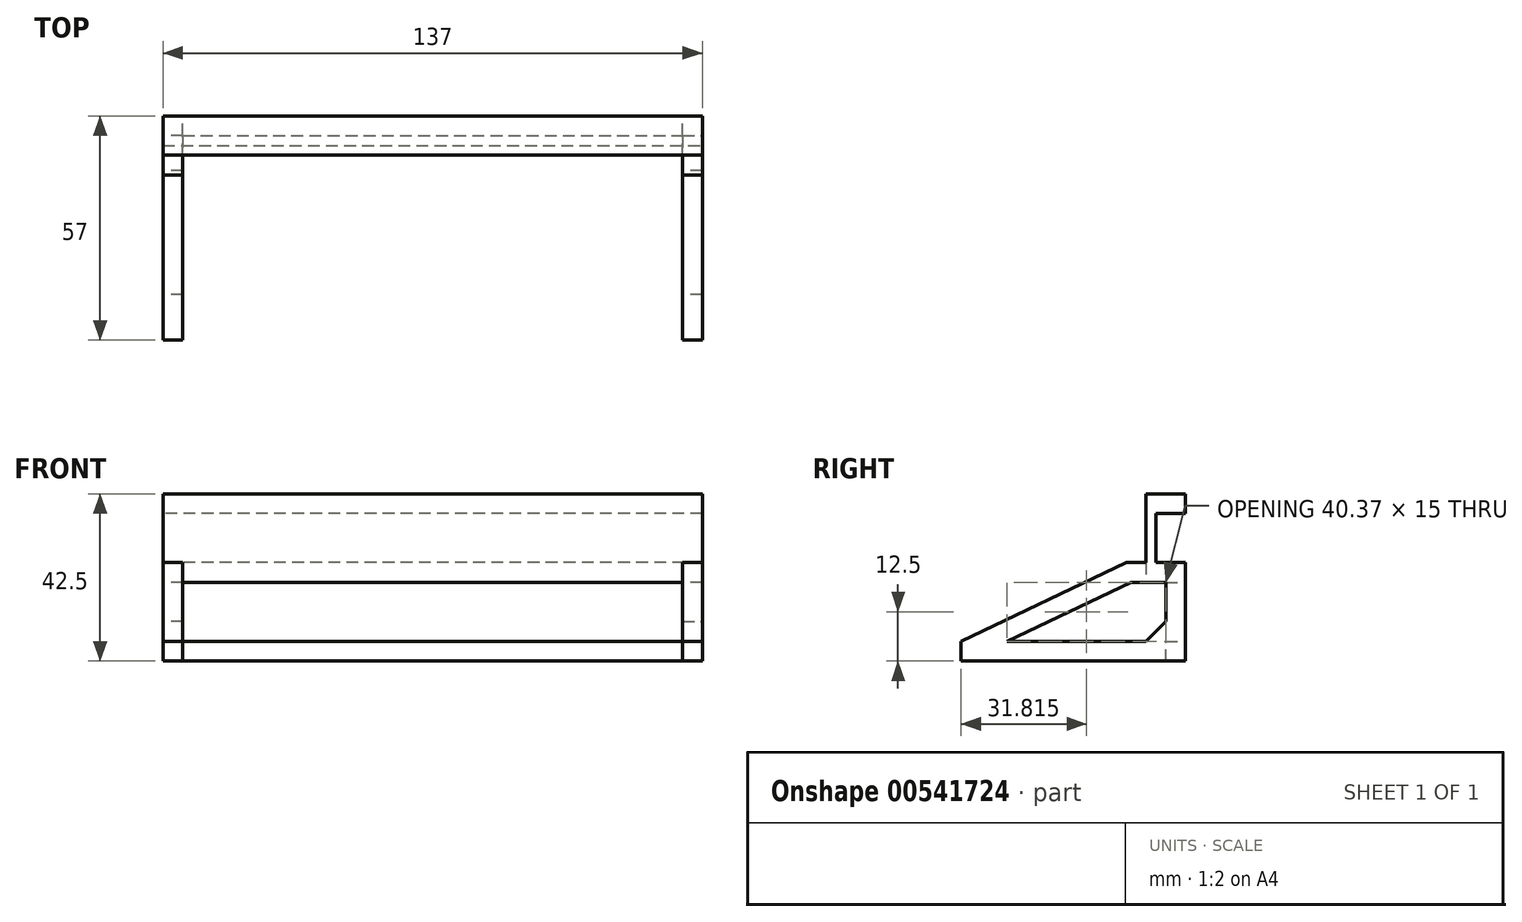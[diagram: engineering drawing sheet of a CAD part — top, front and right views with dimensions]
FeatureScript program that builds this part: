
annotation { "Feature Type Name" : "Feature", "Feature Type Description" : "" }
export const myFeature = defineFeature(function(context is Context, id is Id, definition is map)
    precondition{}
    {
        {
            var Q0;
            Q0=qCreatedBy(makeId("Top.planeOp"),FACE);
            var sketch = newSketch(context, id + "F0", { "sketchPlane" : qUnion([Q0])});
            skLineSegment(sketch, "E0.bottom", {"start": v(68.5, 30) * mm, "end": v(-68.5, 30) * mm});
            skLineSegment(sketch, "E0.top", {"start": v(68.5, -30) * mm, "end": v(-68.5, -30) * mm});
            skLineSegment(sketch, "E0.left", {"start": v(68.5, 30) * mm, "end": v(68.5, -30) * mm});
            skLineSegment(sketch, "E0.right", {"start": v(-68.5, 30) * mm, "end": v(-68.5, -30) * mm});
            skPoint(sketch, "E0.middle", {"position": v(0, 0) * mm});
            skPoint(sketch, "E1", {"position": v(-63.5, 25) * mm});
            skPoint(sketch, "E2", {"position": v(63.5, -25) * mm});
            skLineSegment(sketch, "E3.bottom", {"start": v(-63.5, 25) * mm, "end": v(63.5, 25) * mm});
            skLineSegment(sketch, "E3.top", {"start": v(-63.5, -25) * mm, "end": v(63.5, -25) * mm});
            skLineSegment(sketch, "E3.left", {"start": v(-63.5, 25) * mm, "end": v(-63.5, -25) * mm});
            skLineSegment(sketch, "E3.right", {"start": v(63.5, 25) * mm, "end": v(63.5, -25) * mm});
            skSolve(sketch);
        }
        {
            var Q0;
            Q0=makeQuery(id+"F0.imprint","IMPRINT",FACE,{"disambiguationData":[TD([[makeQuery(id+"F0.imprint","IMPRINT",EDGE,{"derivedFrom":sQuery(id+"F0.wireOp",EDGE,"E0.bottom")}),1.0]])]});
            extrude(context, id + "F1", {"entities" : qUnion([Q0]), "depth" : 25 * mm, "offsetDistance" : 25 * mm});
        }
        {
            var Q0;
            Q0=makeQuery(id+"F1.opExtrude","SWEPT_FACE",FACE,{"disambiguationData":[OSD([sQuery(id+"F0.wireOp",EDGE,"E0.right")])]});
            var sketch = newSketch(context, id + "F2", { "sketchPlane" : qUnion([Q0])});
            skPoint(sketch, "E4", {"position": v(30, 5) * mm});
            skPoint(sketch, "E5", {"position": v(-25, 25) * mm});
            skLineSegment(sketch, "E6", {"start": v(-25, 25) * mm, "end": v(30, 5) * mm});
            skSolve(sketch);
        }
        {
            var Q0;
            {var subQ0=sQuery(id+"F2.wireOp",EDGE,"E6");Q0=makeQuery(id+"F2.imprint","IMPRINT",FACE,{"disambiguationData":[TD([[makeQuery(id+"F2.imprint","IMPRINT",EDGE,{"derivedFrom":subQ0}),1.0]])]});}
            extrude(context, id + "F3", {"entities" : qUnion([Q0]), "operationType" : NewBodyOperationType.REMOVE, "endBound" : BoundingType.THROUGH_ALL, "oppositeDirection" : true, "depth" : 25 * mm, "offsetDistance" : 25 * mm});
        }
        {
            var Q0;
            Q0=makeQuery(id+"F1.opExtrude","SWEPT_FACE",FACE,{"disambiguationData":[OSD([sQuery(id+"F0.wireOp",EDGE,"E0.bottom")])]});
            extrude(context, id + "F4", {"entities" : qUnion([Q0]), "operationType" : NewBodyOperationType.ADD, "depth" : 10 * mm, "offsetDistance" : 25 * mm});
        }
        {
            var Q0;
            {var subQ0=sQuery(id+"F0.wireOp",EDGE,"E0.bottom");Q0=makeQuery(id+"F4.boolean.opBoolean","MERGE",FACE,{"derivedFrom":[makeQuery(id+"F1.opExtrude","CAP_FACE",FACE,{"disambiguationData":[OSD([subQ0,sQuery(id+"F0.wireOp",EDGE,"E0.top"),sQuery(id+"F0.wireOp",EDGE,"E0.left"),sQuery(id+"F0.wireOp",EDGE,"E0.right"),sQuery(id+"F0.wireOp",EDGE,"E3.bottom"),sQuery(id+"F0.wireOp",EDGE,"E3.top"),sQuery(id+"F0.wireOp",EDGE,"E3.left"),sQuery(id+"F0.wireOp",EDGE,"E3.right")])],"isStart":false}),makeQuery(id+"F4.opExtrude","SWEPT_FACE",FACE,{"disambiguationData":[OSD([subQ0]),TDD([makeQuery(id+"F1.opExtrude","CAP_EDGE",EDGE,{"disambiguationData":[OSD([subQ0])],"isStart":false})])]})]});}
            var sketch = newSketch(context, id + "F5", { "sketchPlane" : qUnion([Q0])});
            skPoint(sketch, "E7", {"position": v(-68.5, 32.5) * mm});
            skLineSegment(sketch, "E8", {"start": v(-68.5, 32.5) * mm, "end": v(68.5, 32.5) * mm});
            skSolve(sketch);
        }
        {
            var Q0;
            {var subQ13=sQuery(id+"F5.wireOp",EDGE,"E8");Q0=makeQuery(id+"F5.imprint","IMPRINT",FACE,{"disambiguationData":[TD([[makeQuery(id+"F5.imprint","IMPRINT",EDGE,{"derivedFrom":subQ13}),-1.0]])]});}
            extrude(context, id + "F6", {"entities" : qUnion([Q0]), "operationType" : NewBodyOperationType.ADD, "depth" : 17.5 * mm, "offsetDistance" : 25 * mm});
        }
        {
            var Q0;
            Q0=makeQuery(id+"F6.opExtrude","SWEPT_FACE",FACE,{"disambiguationData":[OSD([sQuery(id+"F5.wireOp",EDGE,"E8")])]});
            var sketch = newSketch(context, id + "F7", { "sketchPlane" : qUnion([Q0])});
            skPoint(sketch, "E9", {"position": v(-68.5, 37.5) * mm});
            skLineSegment(sketch, "E10.bottom", {"start": v(-68.5, 37.5) * mm, "end": v(68.5, 37.5) * mm});
            skLineSegment(sketch, "E10.top", {"start": v(-68.5, 42.5) * mm, "end": v(68.5, 42.5) * mm});
            skLineSegment(sketch, "E10.left", {"start": v(-68.5, 37.5) * mm, "end": v(-68.5, 42.5) * mm});
            skLineSegment(sketch, "E10.right", {"start": v(68.5, 37.5) * mm, "end": v(68.5, 42.5) * mm});
            skSolve(sketch);
        }
        {
            var Q0;
            Q0=makeQuery(id+"F7.imprint","IMPRINT",FACE,{"disambiguationData":[TD([[makeQuery(id+"F7.imprint","IMPRINT",EDGE,{"derivedFrom":sQuery(id+"F7.wireOp",EDGE,"E10.bottom")}),1.0]])]});
            var Q1;
            Q1=makeQuery(id+"F4.opExtrude","CAP_FACE",FACE,{"disambiguationData":[OSD([sQuery(id+"F0.wireOp",EDGE,"E0.bottom")])],"isStart":false});
            extrude(context, id + "F8", {"entities" : qUnion([Q0]), "operationType" : NewBodyOperationType.ADD, "endBound" : BoundingType.UP_TO_SURFACE, "depth" : 25 * mm, "endBoundEntityFace" : qUnion([Q1]), "offsetDistance" : 25 * mm});
        }
        {
            var Q0;
            Q0=makeQuery(id+"F4.opExtrude","CAP_FACE",FACE,{"disambiguationData":[OSD([sQuery(id+"F0.wireOp",EDGE,"E0.bottom")])],"isStart":false});
            var sketch = newSketch(context, id + "F9", { "sketchPlane" : qUnion([Q0])});
            skPoint(sketch, "E11", {"position": v(-63.5, 20) * mm});
            skPoint(sketch, "E12", {"position": v(63.5, 5) * mm});
            skLineSegment(sketch, "E13.bottom", {"start": v(-63.5, 20) * mm, "end": v(63.5, 20) * mm});
            skLineSegment(sketch, "E13.top", {"start": v(-63.5, 5) * mm, "end": v(63.5, 5) * mm});
            skLineSegment(sketch, "E13.left", {"start": v(-63.5, 20) * mm, "end": v(-63.5, 5) * mm});
            skLineSegment(sketch, "E13.right", {"start": v(63.5, 20) * mm, "end": v(63.5, 5) * mm});
            skSolve(sketch);
        }
        {
            var Q0;
            {var subQ0=sQuery(id+"F0.wireOp",EDGE,"E0.left");var subQ1=sQuery(id+"F0.wireOp",EDGE,"E0.bottom");Q0=makeQuery(id+"F8.boolean.opBoolean","MERGE",FACE,{"derivedFrom":[makeQuery(id+"F6.boolean.opBoolean","MERGE",FACE,{"derivedFrom":[makeQuery(id+"F4.boolean.opBoolean","MERGE",FACE,{"derivedFrom":[makeQuery(id+"F1.opExtrude","SWEPT_FACE",FACE,{"disambiguationData":[OSD([subQ0])]}),makeQuery(id+"F4.opExtrude","SWEPT_FACE",FACE,{"disambiguationData":[OSD([subQ1,subQ0])]})]}),makeQuery(id+"F6.opExtrude","SWEPT_FACE",FACE,{"disambiguationData":[OSD([subQ1,subQ0])]})]}),makeQuery(id+"F8.opExtrude","SWEPT_FACE",FACE,{"disambiguationData":[OSD([sQuery(id+"F7.wireOp",EDGE,"E10.left")])]})]});}
            var sketch = newSketch(context, id + "F10", { "sketchPlane" : qUnion([Q0])});
            skPoint(sketch, "E14", {"position": v(-17, 0) * mm});
            skLineSegment(sketch, "E15", {"start": v(-17, 0) * mm, "end": v(-17, 9.73) * mm});
            skSolve(sketch);
        }
        {
            var Q0;
            {var subQ0=sQuery(id+"F10.wireOp",EDGE,"E15");Q0=makeQuery(id+"F10.imprint","IMPRINT",FACE,{"disambiguationData":[TD([[makeQuery(id+"F10.imprint","IMPRINT",EDGE,{"derivedFrom":subQ0}),1.0]])]});}
            extrude(context, id + "F11", {"entities" : qUnion([Q0]), "operationType" : NewBodyOperationType.REMOVE, "endBound" : BoundingType.THROUGH_ALL, "oppositeDirection" : true, "depth" : 25 * mm, "offsetDistance" : 25 * mm});
        }
        {
            var Q0;
            {var subQ3=sQuery(id+"F0.wireOp",EDGE,"E3.bottom");var subQ4=sQuery(id+"F0.wireOp",EDGE,"E0.right");Q0=makeQuery(id+"FVMJIEAKdRelkvC_1.boolean.opBoolean","SPLIT",FACE,{"disambiguationData":[TD([makeQuery(id+"FVMJIEAKdRelkvC_1.opExtrude","SWEPT_FACE",FACE,{"disambiguationData":[OSD([sQuery(id+"Ff6jXWaRgxi8vil_1.wireOp",EDGE,"BFvBPHGJ-g1eL-yhey-g6Zf-fKgrT3vlxnNi")])]})])],"derivedFrom":makeQuery(id+"F6.boolean.opBoolean","MERGE",FACE,{"derivedFrom":[makeQuery(id+"F1.opExtrude","SWEPT_FACE",FACE,{"disambiguationData":[OSD([subQ3])]}),makeQuery(id+"F6.opExtrude","SWEPT_FACE",FACE,{"disambiguationData":[OSD([subQ4,subQ3,sQuery(id+"F2.wireOp",EDGE,"E6")])]})]})});}
            extrude(context, id + "F12", {"entities" : qUnion([Q0]), "operationType" : NewBodyOperationType.REMOVE, "oppositeDirection" : true, "depth" : 5 * mm, "offsetDistance" : 25 * mm});
        }
        {
            var Q0;
            {var subQ0=sQuery(id+"F0.wireOp",EDGE,"E0.right");var subQ1=sQuery(id+"F0.wireOp",EDGE,"E0.bottom");Q0=makeQuery(id+"F8.boolean.opBoolean","MERGE",FACE,{"derivedFrom":[makeQuery(id+"F6.boolean.opBoolean","MERGE",FACE,{"derivedFrom":[makeQuery(id+"F4.boolean.opBoolean","MERGE",FACE,{"derivedFrom":[makeQuery(id+"F1.opExtrude","SWEPT_FACE",FACE,{"disambiguationData":[OSD([subQ0])]}),makeQuery(id+"F4.opExtrude","SWEPT_FACE",FACE,{"disambiguationData":[OSD([subQ1,subQ0])]})]}),makeQuery(id+"F6.opExtrude","SWEPT_FACE",FACE,{"disambiguationData":[OSD([subQ1,subQ0])]})]}),makeQuery(id+"F8.opExtrude","SWEPT_FACE",FACE,{"disambiguationData":[OSD([sQuery(id+"F7.wireOp",EDGE,"E10.right")])]})]});}
            var sketch = newSketch(context, id + "F13", { "sketchPlane" : qUnion([Q0])});
            skPoint(sketch, "E16", {"position": v(17, 5) * mm});
            skLineSegment(sketch, "E17", {"start": v(17, 5) * mm, "end": v(-25, 25) * mm});
            skSolve(sketch);
        }
        {
            var Q0;
            {var subQ0=sQuery(id+"F13.wireOp",EDGE,"E17");Q0=makeQuery(id+"F13.imprint","IMPRINT",FACE,{"disambiguationData":[TD([[makeQuery(id+"F13.imprint","IMPRINT",EDGE,{"derivedFrom":subQ0}),-1.0]])]});}
            extrude(context, id + "F14", {"entities" : qUnion([Q0]), "operationType" : NewBodyOperationType.REMOVE, "endBound" : BoundingType.THROUGH_ALL, "oppositeDirection" : true, "depth" : 25 * mm, "offsetDistance" : 25 * mm});
        }
        {
            var Q0;
            Q0=makeQuery(id+"F9.imprint","IMPRINT",FACE,{"disambiguationData":[TD([[makeQuery(id+"F9.imprint","IMPRINT",EDGE,{"derivedFrom":sQuery(id+"F9.wireOp",EDGE,"E13.bottom")}),-1.0]])]});
            extrude(context, id + "F15", {"entities" : qUnion([Q0]), "operationType" : NewBodyOperationType.REMOVE, "endBound" : BoundingType.THROUGH_ALL, "oppositeDirection" : true, "depth" : 25 * mm, "offsetDistance" : 25 * mm});
        }
        {
            var Q0;
            {var subQ0=sQuery(id+"F0.wireOp",EDGE,"E0.right");var subQ1=sQuery(id+"F0.wireOp",EDGE,"E0.bottom");Q0=makeQuery(id+"F8.boolean.opBoolean","MERGE",FACE,{"derivedFrom":[makeQuery(id+"F6.boolean.opBoolean","MERGE",FACE,{"derivedFrom":[makeQuery(id+"F4.boolean.opBoolean","MERGE",FACE,{"derivedFrom":[makeQuery(id+"F1.opExtrude","SWEPT_FACE",FACE,{"disambiguationData":[OSD([subQ0])]}),makeQuery(id+"F4.opExtrude","SWEPT_FACE",FACE,{"disambiguationData":[OSD([subQ1,subQ0])]})]}),makeQuery(id+"F6.opExtrude","SWEPT_FACE",FACE,{"disambiguationData":[OSD([subQ1,subQ0])]})]}),makeQuery(id+"F8.opExtrude","SWEPT_FACE",FACE,{"disambiguationData":[OSD([sQuery(id+"F7.wireOp",EDGE,"E10.right")])]})]});}
            var sketch = newSketch(context, id + "F16", { "sketchPlane" : qUnion([Q0])});
            skPoint(sketch, "E18", {"position": v(16.01, 1.09) * mm});
            skPoint(sketch, "E19", {"position": v(-9.28, 11.97) * mm});
            skLineSegment(sketch, "E20", {"start": v(-9.28, 11.97) * mm, "end": v(-36.63, 25) * mm});
            skLineSegment(sketch, "E21", {"start": v(-9.28, 11.97) * mm, "end": v(15.87, 0) * mm});
            skPoint(sketch, "E22", {"position": v(-35, 20) * mm});
            skPoint(sketch, "E23", {"position": v(-35, 5) * mm});
            skLineSegment(sketch, "E24", {"start": v(-35, 5) * mm, "end": v(5.37, 5) * mm});
            skLineSegment(sketch, "E25", {"start": v(-35, 5) * mm, "end": v(-35, 20) * mm});
            skLineSegment(sketch, "E26", {"start": v(-35, 20) * mm, "end": v(-26.13, 20) * mm});
            skSolve(sketch);
        }
        {
            var Q0;
            {var subQ0=sQuery(id+"F16.wireOp",EDGE,"E24");Q0=makeQuery(id+"F16.imprint","IMPRINT",FACE,{"disambiguationData":[TD([[makeQuery(id+"F16.imprint","IMPRINT",EDGE,{"derivedFrom":subQ0}),1.0]])]});}
            extrude(context, id + "F17", {"entities" : qUnion([Q0]), "operationType" : NewBodyOperationType.REMOVE, "endBound" : BoundingType.THROUGH_ALL, "oppositeDirection" : true, "depth" : 25 * mm, "offsetDistance" : 25 * mm});
        }
        {
            var Q0;
            {var subQ3=sQuery(id+"F0.wireOp",EDGE,"E3.bottom");var subQ4=sQuery(id+"F0.wireOp",EDGE,"E0.right");Q0=makeQuery(id+"F15.boolean.opBoolean","SPLIT",FACE,{"disambiguationData":[TD([makeQuery(id+"F15.opExtrude","SWEPT_FACE",FACE,{"disambiguationData":[OSD([sQuery(id+"F9.wireOp",EDGE,"E13.top")])]})])],"derivedFrom":makeQuery(id+"F12.boolean.opBoolean","COPY",FACE,{"derivedFrom":makeQuery(id+"F12.opExtrude","CAP_FACE",FACE,{"disambiguationData":[OSD([subQ4,subQ3,sQuery(id+"F2.wireOp",EDGE,"E6")])],"isStart":false})})});}
            var Q1;
            {var subQ1=sQuery(id+"F0.wireOp",EDGE,"E0.right");Q1=makeQuery(id+"F17.boolean.opBoolean","COPY",FACE,{"disambiguationData":[TD([makeQuery(id+"F1.opExtrude","SWEPT_FACE",FACE,{"disambiguationData":[OSD([subQ1])]})])],"derivedFrom":makeQuery(id+"F17.opExtrude","SWEPT_FACE",FACE,{"disambiguationData":[OSD([sQuery(id+"F16.wireOp",EDGE,"E25")])]})});}
            extrude(context, id + "F18", {"entities" : qUnion([Q0]), "operationType" : NewBodyOperationType.REMOVE, "endBound" : BoundingType.UP_TO_SURFACE, "oppositeDirection" : true, "depth" : 25 * mm, "endBoundEntityFace" : qUnion([Q1]), "offsetDistance" : 25 * mm});
        }
        {
            var Q0;
            {var subQ0=sQuery(id+"F0.wireOp",EDGE,"E0.right");var subQ1=sQuery(id+"F0.wireOp",EDGE,"E0.bottom");Q0=makeQuery(id+"F8.boolean.opBoolean","MERGE",FACE,{"derivedFrom":[makeQuery(id+"F6.boolean.opBoolean","MERGE",FACE,{"derivedFrom":[makeQuery(id+"F4.boolean.opBoolean","MERGE",FACE,{"derivedFrom":[makeQuery(id+"F1.opExtrude","SWEPT_FACE",FACE,{"disambiguationData":[OSD([subQ0])]}),makeQuery(id+"F4.opExtrude","SWEPT_FACE",FACE,{"disambiguationData":[OSD([subQ1,subQ0])]})]}),makeQuery(id+"F6.opExtrude","SWEPT_FACE",FACE,{"disambiguationData":[OSD([subQ1,subQ0])]})]}),makeQuery(id+"F8.opExtrude","SWEPT_FACE",FACE,{"disambiguationData":[OSD([sQuery(id+"F7.wireOp",EDGE,"E10.right")])]})]});}
            var sketch = newSketch(context, id + "F19", { "sketchPlane" : qUnion([Q0])});
            skPoint(sketch, "E27", {"position": v(-35, 10) * mm});
            skPoint(sketch, "E28", {"position": v(-30, 5) * mm});
            skLineSegment(sketch, "E29", {"start": v(-30, 5) * mm, "end": v(-35, 10) * mm});
            skSolve(sketch);
        }
        {
            var Q0;
            {var subQ0=sQuery(id+"F19.wireOp",EDGE,"E29");Q0=makeQuery(id+"F19.imprint","IMPRINT",FACE,{"disambiguationData":[TD([[makeQuery(id+"F19.imprint","IMPRINT",EDGE,{"derivedFrom":subQ0}),1.0]])]});}
            extrude(context, id + "F20", {"entities" : qUnion([Q0]), "operationType" : NewBodyOperationType.ADD, "oppositeDirection" : true, "depth" : 5 * mm, "offsetDistance" : 25 * mm});
        }
        {
            var Q0;
            {var subQ0=sQuery(id+"F0.wireOp",EDGE,"E0.left");var subQ1=sQuery(id+"F0.wireOp",EDGE,"E0.bottom");Q0=makeQuery(id+"F8.boolean.opBoolean","MERGE",FACE,{"derivedFrom":[makeQuery(id+"F6.boolean.opBoolean","MERGE",FACE,{"derivedFrom":[makeQuery(id+"F4.boolean.opBoolean","MERGE",FACE,{"derivedFrom":[makeQuery(id+"F1.opExtrude","SWEPT_FACE",FACE,{"disambiguationData":[OSD([subQ0])]}),makeQuery(id+"F4.opExtrude","SWEPT_FACE",FACE,{"disambiguationData":[OSD([subQ1,subQ0])]})]}),makeQuery(id+"F6.opExtrude","SWEPT_FACE",FACE,{"disambiguationData":[OSD([subQ1,subQ0])]})]}),makeQuery(id+"F8.opExtrude","SWEPT_FACE",FACE,{"disambiguationData":[OSD([sQuery(id+"F7.wireOp",EDGE,"E10.left")])]})]});}
            var sketch = newSketch(context, id + "F21", { "sketchPlane" : qUnion([Q0])});
            skPoint(sketch, "E30", {"position": v(30, 5) * mm});
            skPoint(sketch, "E31", {"position": v(35, 10) * mm});
            skLineSegment(sketch, "E32", {"start": v(30, 5) * mm, "end": v(35, 10) * mm});
            skSolve(sketch);
        }
        {
            var Q0;
            {var subQ0=sQuery(id+"F21.wireOp",EDGE,"E32");Q0=makeQuery(id+"F21.imprint","IMPRINT",FACE,{"disambiguationData":[TD([[makeQuery(id+"F21.imprint","IMPRINT",EDGE,{"derivedFrom":subQ0}),-1.0]])]});}
            extrude(context, id + "F22", {"entities" : qUnion([Q0]), "operationType" : NewBodyOperationType.ADD, "oppositeDirection" : true, "depth" : 5 * mm, "offsetDistance" : 25 * mm});
        }
    });
